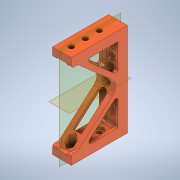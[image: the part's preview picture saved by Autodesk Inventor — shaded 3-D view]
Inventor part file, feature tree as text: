
AUTODESK INVENTOR PART (.ipt)
format: ipt  version: 2020 (Build 240168000, 168)  size: 618,496 bytes
history: native  units: in
note: dims shown in document units (in); Inventor stores cm internally (conversion verified against a paired STEP export)
features: extrude x14, sketch x12, projected_geometry x7, plane x5, fillet x4, chamfer x2, mirror x1
ambient origin geometry x8: Origin, YZ Plane, XZ Plane, XY Plane, X Axis, Y Axis, Z Axis, Center Point
bodies: Solid1 (feature_tree)
feature tree (45):
  extrude  "Extrusion1"  Depth=5.0in
  extrude  "Extrusion2"  Depth=0.5in
  fillet  "Fillet1"  Radius=0.5in
  extrude  "Extrusion3"  Depth=0.05in
  fillet  "Fillet2"  Radius=0.25in
  extrude  "Extrusion4"  Depth=0.5in
  plane  "Work Plane1"
  extrude  "Extrusion5"  Depth=2.5in
  extrude  "Extrusion6"  TaperAngle=0.0deg  [1 undecoded]
  plane  "Work Plane2"
  extrude  "Extrusion7"  Depth=0.4532in
  plane  "Work Plane3"
  extrude  "Extrusion8"  Depth=0.25in TaperAngle=0.0deg
  extrude  "Extrusion10"  Depth=0.5in
  plane  "Work Plane4"
  plane  "Work Plane5"
  extrude  "Extrusion11"  Depth=0.3937in
  chamfer  "Chamfer1"  [1 undecoded]
  extrude  "Extrusion12"  Depth=0.4532in
  extrude  "Extrusion13"  [1 undecoded]
  chamfer  "Chamfer2"  Distance=0.4532in
  fillet  "Fillet3"  Radius=2.5in
  fillet  "Fillet4"  Radius=0.375in
  extrude  "Extrusion14"  Depth=0.125in TaperAngle=0.0deg
  extrude  "Extrusion15"  [1 undecoded]
  mirror  "Mirror2"
  sketch  "Sketch1"  dims[d0=1.0in d1=5.0in]
  sketch  "Sketch2"  dims[d2=3.0in d3=0.0in d4=0.5in d5=0.5in]
  sketch  "Sketch3"  dims[d6=0.0in d7=0.0in d8=0.05in d9=0.25in]
  sketch  "Sketch4"  dims[d10=1.0in d11=0.0in d12=0.5in d13=0.125in]
  sketch  "Sketch6"  dims[d14=0.2in d16=2.5in]
  sketch  "Sketch8"  dims[d17=4.3307in d19=0.5in d20=0.3937in d22=1.0in d24=0.0in d25=0.0in]
  sketch  "Sketch10"  dims[d26=-0.25in d27=0.4532in]
  sketch  "Sketch11"  dims[d28=3.5433in d30=0.5in d31=0.3937in d33=1.0in d35=0.25in d36=0.0in]
  sketch  "Sketch12"  dims[d37=1.0in d38=0.5in]
  projected_geometry  "Projected Loop1"
  projected_geometry  "Projected Loop2"
  projected_geometry  "Projected Loop3"
  sketch  "Sketch13"  dims[d39=0.2656in d40=1.1811in d42=0.75in d43=0.3937in d45=1.0in d47=0.0in d48=0.0in]
  projected_geometry  "Projected Loop4"
  projected_geometry  "Projected Loop5"
  projected_geometry  "Projected Loop6"
  sketch  "Sketch14"  dims[d49=-0.25in d50=0.4532in]
  sketch  "Sketch15"  dims[d51=2.5in d52=0.0in d53=-0.25in d54=0.4532in d55=2.5in d56=0.0in d59=0.375in d60=0.26in d61=0.0in d62=-0.5in d63=0.375in d64=0.375in d65=0.375in d66=0.4532in d67=0.0in d68=0.125in d69=0.125in d70=45.0deg d71=0.4532in d72=0.0in d73=0.975in d74=0.0in d75=0.125in d76=0.125in d77=45.0deg d78=0.125in d79=0.175in d80=1.0in d81=0.0in d82=1.0in d83=0.0in]
  projected_geometry  "Projected Loop7"
note: 4 required parameter values undecoded (feature->parameter linkage not recoverable at this tier; creation-order binding heuristic only, values carry confidence <= 0.55)
